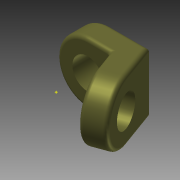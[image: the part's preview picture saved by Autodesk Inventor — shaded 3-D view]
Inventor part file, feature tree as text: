
AUTODESK INVENTOR PART (.ipt)
format: ipt  version: 2011 SP2 (Build 150309200, 309)  size: 153,088 bytes
history: native  units: mm
features: fillet x3, other x3, hole x2, extrude x1, sketch x1
ambient origin geometry x8: Origin, YZ Plane, XZ Plane, XY Plane, X Axis, Y Axis, Z Axis, Center Point
bodies: Solid1 (feature_tree)
feature tree (10):
  extrude  "Extrusion1"  Depth=12.0mm
  fillet  "Fillet1"  Radius=9.599311mm
  hole  "Hole1"  [1 undecoded]
  hole  "Hole2"  [1 undecoded]
  fillet  "Fillet2"  Radius=10.0mm
  fillet  "Fillet3"  Radius=10.0mm
  other  "Work Point1"
  sketch  "Sketch1"  dims[d0=36.0mm d1=12.0mm d2=9.599311mm d3=32.0mm d4=0.0mm d5=16.0mm d6=10.0mm d7=10.0mm d8=16.0mm d9=6.0mm d10=4.0mm d11=2.0mm d12=90.0deg d13=8.0mm d14=20.594885mm d15=10.0mm d16=10.0mm d17=16.0mm d18=6.0mm d19=4.0mm d20=2.0mm d21=90.0deg d22=8.0mm d23=20.594885mm d24=2.0mm d25=2.0mm]
  other  "Work Axis1"
  other  "Work Axis2"
note: 2 required parameter values undecoded (feature->parameter linkage not recoverable at this tier; creation-order binding heuristic only, values carry confidence <= 0.55)
